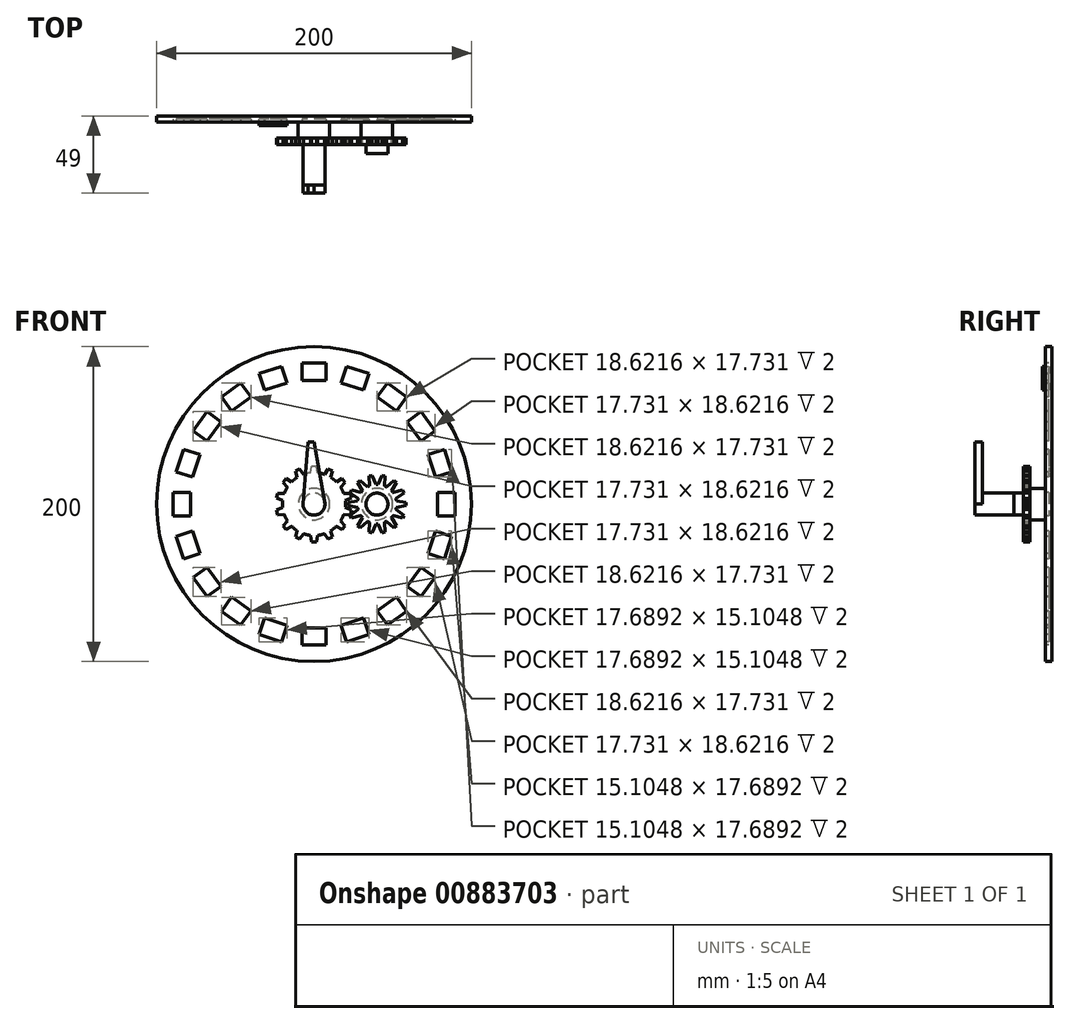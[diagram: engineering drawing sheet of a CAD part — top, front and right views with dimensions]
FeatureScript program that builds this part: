
annotation { "Feature Type Name" : "Feature", "Feature Type Description" : "" }
export const myFeature = defineFeature(function(context is Context, id is Id, definition is map)
    precondition{}
    {
        {
            var Q0;
            Q0=qCreatedBy(makeId("Front.planeOp"),FACE);
            var sketch = newSketch(context, id + "F0", { "sketchPlane" : qUnion([Q0])});
            skCircle(sketch, "E0", {"center": v(0, 0) * mm, "radius": 100 * mm});
            skSolve(sketch);
        }
        {
            var Q0;
            Q0 = qSketchRegion(id + "F0", true);
            extrude(context, id + "F1", {"entities" : qUnion([Q0]), "depth" : 4 * mm, "offsetDistance" : 25 * mm});
        }
        {
            var Q0;
            Q0=makeQuery(id+"F1.opExtrude","CAP_FACE",FACE,{"disambiguationData":[OSD([sQuery(id+"F0.wireOp",EDGE,"E0")])],"isStart":false});
            var sketch = newSketch(context, id + "F2", { "sketchPlane" : qUnion([Q0])});
            skCircle(sketch, "E1", {"center": v(0, 0) * mm, "radius": 10 * mm});
            skCircle(sketch, "E2", {"center": v(0, 0) * mm, "radius": 7 * mm});
            skCircle(sketch, "E3", {"center": v(40, 0) * mm, "radius": 10 * mm});
            skCircle(sketch, "E4", {"center": v(40, 0) * mm, "radius": 7 * mm});
            skSolve(sketch);
        }
        {
            var Q0;
            Q0 = qSketchRegion(id + "F2", true);
            extrude(context, id + "F3", {"entities" : qUnion([Q0]), "operationType" : NewBodyOperationType.ADD, "depth" : 10 * mm, "offsetDistance" : 25 * mm});
        }
        {
            var Q0;
            Q0=makeQuery(id+"F3.boolean.opBoolean","SPLIT",FACE,{"disambiguationData":[TD([makeQuery(id+"F3.opExtrude","SWEPT_FACE",FACE,{"disambiguationData":[OSD([sQuery(id+"F2.wireOp",EDGE,"E2")])]})])],"derivedFrom":makeQuery(id+"F1.opExtrude","CAP_FACE",FACE,{"disambiguationData":[OSD([sQuery(id+"F0.wireOp",EDGE,"E0")])],"isStart":false})});
            extrude(context, id + "F4", {"entities" : qUnion([Q0]), "depth" : 40 * mm, "offsetDistance" : 25 * mm});
        }
        {
            var Q0;
            Q0=makeQuery(id+"F3.boolean.opBoolean","SPLIT",FACE,{"disambiguationData":[TD([makeQuery(id+"F3.opExtrude","SWEPT_FACE",FACE,{"disambiguationData":[OSD([sQuery(id+"F2.wireOp",EDGE,"E4")])]})])],"derivedFrom":makeQuery(id+"F1.opExtrude","CAP_FACE",FACE,{"disambiguationData":[OSD([sQuery(id+"F0.wireOp",EDGE,"E0")])],"isStart":false})});
            extrude(context, id + "F5", {"entities" : qUnion([Q0]), "depth" : 20 * mm, "offsetDistance" : 25 * mm});
        }
        {
            var Q0;
            Q0=makeQuery(id+"F3.opExtrude","CAP_FACE",FACE,{"disambiguationData":[OSD([sQuery(id+"F2.wireOp",EDGE,"E1"),sQuery(id+"F2.wireOp",EDGE,"E2")])],"isStart":false});
            var sketch = newSketch(context, id + "F6", { "sketchPlane" : qUnion([Q0])});
            skCircle(sketch, "E5", {"center": v(0, 0) * mm, "radius": 20 * mm});
            skLineSegment(sketch, "E6", {"start": v(2.23, 19.88) * mm, "end": v(1.5, 24) * mm});
            skLineSegment(sketch, "E7", {"start": v(1.5, 24) * mm, "end": v(0, 24) * mm});
            skLineSegment(sketch, "E8.MirrorCS", {"start": v(-1.5, 24) * mm, "end": v(0, 24) * mm});
            skLineSegment(sketch, "E9.MirrorCS", {"start": v(-2.23, 19.88) * mm, "end": v(-1.5, 24) * mm});
            skLineSegment(sketch, "E10.1.0", {"start": v(-10.63, 16.94) * mm, "end": v(-11.76, 20.97) * mm});
            skLineSegment(sketch, "E10.1.1", {"start": v(-11.76, 20.97) * mm, "end": v(-10.41, 21.62) * mm});
            skLineSegment(sketch, "E10.1.2", {"start": v(-9.06, 22.27) * mm, "end": v(-10.41, 21.62) * mm});
            skLineSegment(sketch, "E10.1.3", {"start": v(-6.62, 18.87) * mm, "end": v(-9.06, 22.27) * mm});
            skLineSegment(sketch, "E10.2.0", {"start": v(-16.93, 10.65) * mm, "end": v(-19.7, 13.8) * mm});
            skLineSegment(sketch, "E10.2.1", {"start": v(-19.7, 13.8) * mm, "end": v(-18.76, 14.96) * mm});
            skLineSegment(sketch, "E10.2.2", {"start": v(-17.83, 16.14) * mm, "end": v(-18.76, 14.96) * mm});
            skLineSegment(sketch, "E10.2.3", {"start": v(-14.15, 14.13) * mm, "end": v(-17.83, 16.14) * mm});
            skLineSegment(sketch, "E11.1.3.0", {"start": v(-19.87, 2.25) * mm, "end": v(-23.73, 3.88) * mm});
            skLineSegment(sketch, "E11.3.3.0", {"start": v(-23.73, 3.88) * mm, "end": v(-23.4, 5.34) * mm});
            skLineSegment(sketch, "E11.6.3.0", {"start": v(-23.06, 6.8) * mm, "end": v(-23.4, 5.34) * mm});
            skLineSegment(sketch, "E11.9.3.0", {"start": v(-18.88, 6.6) * mm, "end": v(-23.06, 6.8) * mm});
            skLineSegment(sketch, "E11.1.4.0", {"start": v(-18.88, -6.6) * mm, "end": v(-23.06, -6.8) * mm});
            skLineSegment(sketch, "E11.3.4.0", {"start": v(-23.06, -6.8) * mm, "end": v(-23.4, -5.34) * mm});
            skLineSegment(sketch, "E11.6.4.0", {"start": v(-23.73, -3.88) * mm, "end": v(-23.4, -5.34) * mm});
            skLineSegment(sketch, "E11.9.4.0", {"start": v(-19.87, -2.25) * mm, "end": v(-23.73, -3.88) * mm});
            skLineSegment(sketch, "E11.1.5.0", {"start": v(-14.15, -14.13) * mm, "end": v(-17.83, -16.14) * mm});
            skLineSegment(sketch, "E11.3.5.0", {"start": v(-17.83, -16.14) * mm, "end": v(-18.76, -14.96) * mm});
            skLineSegment(sketch, "E11.6.5.0", {"start": v(-19.7, -13.8) * mm, "end": v(-18.76, -14.96) * mm});
            skLineSegment(sketch, "E11.9.5.0", {"start": v(-16.93, -10.65) * mm, "end": v(-19.7, -13.8) * mm});
            skLineSegment(sketch, "E11.1.6.0", {"start": v(-6.62, -18.87) * mm, "end": v(-9.06, -22.27) * mm});
            skLineSegment(sketch, "E11.3.6.0", {"start": v(-9.06, -22.27) * mm, "end": v(-10.41, -21.62) * mm});
            skLineSegment(sketch, "E11.6.6.0", {"start": v(-11.76, -20.97) * mm, "end": v(-10.41, -21.62) * mm});
            skLineSegment(sketch, "E11.9.6.0", {"start": v(-10.63, -16.94) * mm, "end": v(-11.76, -20.97) * mm});
            skLineSegment(sketch, "E11.1.7.0", {"start": v(2.23, -19.88) * mm, "end": v(1.5, -24) * mm});
            skLineSegment(sketch, "E11.3.7.0", {"start": v(1.5, -24) * mm, "end": v(0, -24) * mm});
            skLineSegment(sketch, "E11.6.7.0", {"start": v(-1.5, -24) * mm, "end": v(0, -24) * mm});
            skLineSegment(sketch, "E11.9.7.0", {"start": v(-2.23, -19.88) * mm, "end": v(-1.5, -24) * mm});
            skLineSegment(sketch, "E11.1.8.0", {"start": v(10.63, -16.94) * mm, "end": v(11.76, -20.97) * mm});
            skLineSegment(sketch, "E11.3.8.0", {"start": v(11.76, -20.97) * mm, "end": v(10.41, -21.62) * mm});
            skLineSegment(sketch, "E11.6.8.0", {"start": v(9.06, -22.27) * mm, "end": v(10.41, -21.62) * mm});
            skLineSegment(sketch, "E11.9.8.0", {"start": v(6.62, -18.87) * mm, "end": v(9.06, -22.27) * mm});
            skLineSegment(sketch, "E11.1.9.0", {"start": v(16.93, -10.65) * mm, "end": v(19.7, -13.8) * mm});
            skLineSegment(sketch, "E11.3.9.0", {"start": v(19.7, -13.8) * mm, "end": v(18.76, -14.96) * mm});
            skLineSegment(sketch, "E11.6.9.0", {"start": v(17.83, -16.14) * mm, "end": v(18.76, -14.96) * mm});
            skLineSegment(sketch, "E11.9.9.0", {"start": v(14.15, -14.13) * mm, "end": v(17.83, -16.14) * mm});
            skLineSegment(sketch, "E12.1.10.0", {"start": v(19.87, -2.25) * mm, "end": v(23.73, -3.88) * mm});
            skLineSegment(sketch, "E12.3.10.0", {"start": v(23.73, -3.88) * mm, "end": v(23.4, -5.34) * mm});
            skLineSegment(sketch, "E12.6.10.0", {"start": v(23.06, -6.8) * mm, "end": v(23.4, -5.34) * mm});
            skLineSegment(sketch, "E12.9.10.0", {"start": v(18.88, -6.6) * mm, "end": v(23.06, -6.8) * mm});
            skLineSegment(sketch, "E12.1.11.0", {"start": v(18.88, 6.6) * mm, "end": v(23.06, 6.8) * mm});
            skLineSegment(sketch, "E12.3.11.0", {"start": v(23.06, 6.8) * mm, "end": v(23.4, 5.34) * mm});
            skLineSegment(sketch, "E12.6.11.0", {"start": v(23.73, 3.88) * mm, "end": v(23.4, 5.34) * mm});
            skLineSegment(sketch, "E12.9.11.0", {"start": v(19.87, 2.25) * mm, "end": v(23.73, 3.88) * mm});
            skLineSegment(sketch, "E12.1.12.0", {"start": v(14.15, 14.13) * mm, "end": v(17.83, 16.14) * mm});
            skLineSegment(sketch, "E12.3.12.0", {"start": v(17.83, 16.14) * mm, "end": v(18.76, 14.96) * mm});
            skLineSegment(sketch, "E12.6.12.0", {"start": v(19.7, 13.8) * mm, "end": v(18.76, 14.96) * mm});
            skLineSegment(sketch, "E12.9.12.0", {"start": v(16.93, 10.65) * mm, "end": v(19.7, 13.8) * mm});
            skLineSegment(sketch, "E12.1.13.0", {"start": v(6.62, 18.87) * mm, "end": v(9.06, 22.27) * mm});
            skLineSegment(sketch, "E12.3.13.0", {"start": v(9.06, 22.27) * mm, "end": v(10.41, 21.62) * mm});
            skLineSegment(sketch, "E12.6.13.0", {"start": v(11.76, 20.97) * mm, "end": v(10.41, 21.62) * mm});
            skLineSegment(sketch, "E12.9.13.0", {"start": v(10.63, 16.94) * mm, "end": v(11.76, 20.97) * mm});
            skSolve(sketch);
        }
        {
            var Q0;
            Q0 = qSketchRegion(id + "F6", true);
            extrude(context, id + "F7", {"entities" : qUnion([Q0]), "operationType" : NewBodyOperationType.ADD, "depth" : 4 * mm, "offsetDistance" : 25 * mm});
        }
        {
            var Q0;
            Q0=makeQuery(id+"F3.opExtrude","CAP_FACE",FACE,{"disambiguationData":[OSD([sQuery(id+"F2.wireOp",EDGE,"E3"),sQuery(id+"F2.wireOp",EDGE,"E4")])],"isStart":false});
            var sketch = newSketch(context, id + "F8", { "sketchPlane" : qUnion([Q0])});
            skCircle(sketch, "E13", {"center": v(40, 0) * mm, "radius": 12.5 * mm});
            skLineSegment(sketch, "E14", {"start": v(27.67, 2.08) * mm, "end": v(21.53, 1) * mm});
            skLineSegment(sketch, "E15", {"start": v(21.53, 1) * mm, "end": v(21.53, 0) * mm});
            skLineSegment(sketch, "E16.MirrorCS", {"start": v(21.53, -1) * mm, "end": v(21.53, 0) * mm});
            skLineSegment(sketch, "E17.MirrorCS", {"start": v(27.67, -2.08) * mm, "end": v(21.53, -1) * mm});
            skLineSegment(sketch, "E18.1.0", {"start": v(29.8, -7.23) * mm, "end": v(23.8, -8.92) * mm});
            skLineSegment(sketch, "E18.1.1", {"start": v(23.8, -8.92) * mm, "end": v(23.36, -8.02) * mm});
            skLineSegment(sketch, "E18.1.2", {"start": v(22.92, -7.11) * mm, "end": v(23.36, -8.02) * mm});
            skLineSegment(sketch, "E18.1.3", {"start": v(28, -3.47) * mm, "end": v(22.92, -7.11) * mm});
            skLineSegment(sketch, "E18.2.0", {"start": v(33.94, -10.94) * mm, "end": v(29.26, -15.07) * mm});
            skLineSegment(sketch, "E18.2.1", {"start": v(29.26, -15.07) * mm, "end": v(28.48, -14.44) * mm});
            skLineSegment(sketch, "E18.2.2", {"start": v(27.7, -13.82) * mm, "end": v(28.48, -14.44) * mm});
            skLineSegment(sketch, "E18.2.3", {"start": v(30.69, -8.34) * mm, "end": v(27.7, -13.82) * mm});
            skLineSegment(sketch, "E19.2.3.0", {"start": v(39.29, -12.48) * mm, "end": v(36.86, -18.23) * mm});
            skLineSegment(sketch, "E19.3.3.0", {"start": v(36.86, -18.23) * mm, "end": v(35.89, -18) * mm});
            skLineSegment(sketch, "E19.6.3.0", {"start": v(34.91, -17.79) * mm, "end": v(35.89, -18) * mm});
            skLineSegment(sketch, "E19.9.3.0", {"start": v(35.23, -11.55) * mm, "end": v(34.91, -17.79) * mm});
            skLineSegment(sketch, "E19.2.4.0", {"start": v(44.77, -11.55) * mm, "end": v(45.09, -17.79) * mm});
            skLineSegment(sketch, "E19.3.4.0", {"start": v(45.09, -17.79) * mm, "end": v(44.11, -18) * mm});
            skLineSegment(sketch, "E19.6.4.0", {"start": v(43.14, -18.23) * mm, "end": v(44.11, -18) * mm});
            skLineSegment(sketch, "E19.9.4.0", {"start": v(40.71, -12.48) * mm, "end": v(43.14, -18.23) * mm});
            skLineSegment(sketch, "E20.2.5.0", {"start": v(49.31, -8.34) * mm, "end": v(52.3, -13.82) * mm});
            skLineSegment(sketch, "E20.3.5.0", {"start": v(52.3, -13.82) * mm, "end": v(51.52, -14.44) * mm});
            skLineSegment(sketch, "E20.6.5.0", {"start": v(50.74, -15.07) * mm, "end": v(51.52, -14.44) * mm});
            skLineSegment(sketch, "E20.9.5.0", {"start": v(46.06, -10.94) * mm, "end": v(50.74, -15.07) * mm});
            skLineSegment(sketch, "E20.2.6.0", {"start": v(52, -3.47) * mm, "end": v(57.08, -7.11) * mm});
            skLineSegment(sketch, "E20.3.6.0", {"start": v(57.08, -7.11) * mm, "end": v(56.64, -8.02) * mm});
            skLineSegment(sketch, "E20.6.6.0", {"start": v(56.2, -8.92) * mm, "end": v(56.64, -8.02) * mm});
            skLineSegment(sketch, "E20.9.6.0", {"start": v(50.2, -7.23) * mm, "end": v(56.2, -8.92) * mm});
            skLineSegment(sketch, "E20.2.7.0", {"start": v(52.33, 2.08) * mm, "end": v(58.47, 1) * mm});
            skLineSegment(sketch, "E20.3.7.0", {"start": v(58.47, 1) * mm, "end": v(58.47, 0) * mm});
            skLineSegment(sketch, "E20.6.7.0", {"start": v(58.47, -1) * mm, "end": v(58.47, 0) * mm});
            skLineSegment(sketch, "E20.9.7.0", {"start": v(52.33, -2.08) * mm, "end": v(58.47, -1) * mm});
            skLineSegment(sketch, "E20.2.8.0", {"start": v(50.2, 7.23) * mm, "end": v(56.2, 8.92) * mm});
            skLineSegment(sketch, "E20.3.8.0", {"start": v(56.2, 8.92) * mm, "end": v(56.64, 8.02) * mm});
            skLineSegment(sketch, "E20.6.8.0", {"start": v(57.08, 7.11) * mm, "end": v(56.64, 8.02) * mm});
            skLineSegment(sketch, "E20.9.8.0", {"start": v(52, 3.47) * mm, "end": v(57.08, 7.11) * mm});
            skLineSegment(sketch, "E20.2.9.0", {"start": v(46.06, 10.94) * mm, "end": v(50.74, 15.07) * mm});
            skLineSegment(sketch, "E20.3.9.0", {"start": v(50.74, 15.07) * mm, "end": v(51.52, 14.44) * mm});
            skLineSegment(sketch, "E20.6.9.0", {"start": v(52.3, 13.82) * mm, "end": v(51.52, 14.44) * mm});
            skLineSegment(sketch, "E20.9.9.0", {"start": v(49.31, 8.34) * mm, "end": v(52.3, 13.82) * mm});
            skLineSegment(sketch, "E21.2.10.0", {"start": v(40.71, 12.48) * mm, "end": v(43.14, 18.23) * mm});
            skLineSegment(sketch, "E21.3.10.0", {"start": v(43.14, 18.23) * mm, "end": v(44.11, 18) * mm});
            skLineSegment(sketch, "E21.6.10.0", {"start": v(45.09, 17.79) * mm, "end": v(44.11, 18) * mm});
            skLineSegment(sketch, "E21.9.10.0", {"start": v(44.77, 11.55) * mm, "end": v(45.09, 17.79) * mm});
            skLineSegment(sketch, "E21.2.11.0", {"start": v(35.23, 11.55) * mm, "end": v(34.91, 17.79) * mm});
            skLineSegment(sketch, "E21.3.11.0", {"start": v(34.91, 17.79) * mm, "end": v(35.89, 18) * mm});
            skLineSegment(sketch, "E21.6.11.0", {"start": v(36.86, 18.23) * mm, "end": v(35.89, 18) * mm});
            skLineSegment(sketch, "E21.9.11.0", {"start": v(39.29, 12.48) * mm, "end": v(36.86, 18.23) * mm});
            skLineSegment(sketch, "E21.2.12.0", {"start": v(30.69, 8.34) * mm, "end": v(27.7, 13.82) * mm});
            skLineSegment(sketch, "E21.3.12.0", {"start": v(27.7, 13.82) * mm, "end": v(28.48, 14.44) * mm});
            skLineSegment(sketch, "E21.6.12.0", {"start": v(29.26, 15.07) * mm, "end": v(28.48, 14.44) * mm});
            skLineSegment(sketch, "E21.9.12.0", {"start": v(33.94, 10.94) * mm, "end": v(29.26, 15.07) * mm});
            skLineSegment(sketch, "E21.2.13.0", {"start": v(28, 3.47) * mm, "end": v(22.92, 7.11) * mm});
            skLineSegment(sketch, "E21.3.13.0", {"start": v(22.92, 7.11) * mm, "end": v(23.36, 8.02) * mm});
            skLineSegment(sketch, "E21.6.13.0", {"start": v(23.8, 8.92) * mm, "end": v(23.36, 8.02) * mm});
            skLineSegment(sketch, "E21.9.13.0", {"start": v(29.8, 7.23) * mm, "end": v(23.8, 8.92) * mm});
            skSolve(sketch);
        }
        {
            var Q0;
            Q0 = qSketchRegion(id + "F8", true);
            extrude(context, id + "F9", {"entities" : qUnion([Q0]), "operationType" : NewBodyOperationType.ADD, "depth" : 4 * mm, "offsetDistance" : 25 * mm});
        }
        {
            var Q0;
            {var subQ0=sQuery(id+"F0.wireOp",EDGE,"E0");Q0=makeQuery(id+"F3.boolean.opBoolean","SPLIT",FACE,{"disambiguationData":[TD([makeQuery(id+"F1.opExtrude","SWEPT_FACE",FACE,{"disambiguationData":[OSD([subQ0])]})])],"derivedFrom":makeQuery(id+"F1.opExtrude","CAP_FACE",FACE,{"disambiguationData":[OSD([subQ0])],"isStart":false})});}
            var sketch = newSketch(context, id + "F10", { "sketchPlane" : qUnion([Q0])});
            skLineSegment(sketch, "E22.bottom", {"start": v(7.51, 78.55) * mm, "end": v(-7.51, 78.55) * mm});
            skLineSegment(sketch, "E22.top", {"start": v(7.51, 89.55) * mm, "end": v(-7.51, 89.55) * mm});
            skLineSegment(sketch, "E22.left", {"start": v(7.51, 78.55) * mm, "end": v(7.51, 89.55) * mm});
            skLineSegment(sketch, "E22.right", {"start": v(-7.51, 78.55) * mm, "end": v(-7.51, 89.55) * mm});
            skPoint(sketch, "E22.middle", {"position": v(0, 84.05) * mm});
            skLineSegment(sketch, "E23.1.0", {"start": v(-20.53, 87.49) * mm, "end": v(-34.82, 82.85) * mm});
            skLineSegment(sketch, "E23.1.1", {"start": v(-31.42, 72.38) * mm, "end": v(-34.82, 82.85) * mm});
            skLineSegment(sketch, "E23.1.2", {"start": v(-17.13, 77.03) * mm, "end": v(-20.53, 87.49) * mm});
            skLineSegment(sketch, "E23.1.3", {"start": v(-17.13, 77.03) * mm, "end": v(-31.42, 72.38) * mm});
            skLineSegment(sketch, "E23.2.0", {"start": v(-46.56, 76.86) * mm, "end": v(-58.71, 68.03) * mm});
            skLineSegment(sketch, "E23.2.1", {"start": v(-52.25, 59.13) * mm, "end": v(-58.71, 68.03) * mm});
            skLineSegment(sketch, "E23.2.2", {"start": v(-40.1, 67.96) * mm, "end": v(-46.56, 76.86) * mm});
            skLineSegment(sketch, "E23.2.3", {"start": v(-40.1, 67.96) * mm, "end": v(-52.25, 59.13) * mm});
            skPoint(sketch, "E23.center", {"position": v(0, 0) * mm});
            skLineSegment(sketch, "E24.2.3.0", {"start": v(-68.03, 58.71) * mm, "end": v(-76.86, 46.56) * mm});
            skLineSegment(sketch, "E24.3.3.0", {"start": v(-67.96, 40.1) * mm, "end": v(-76.86, 46.56) * mm});
            skLineSegment(sketch, "E24.6.3.0", {"start": v(-59.13, 52.25) * mm, "end": v(-68.03, 58.71) * mm});
            skLineSegment(sketch, "E24.9.3.0", {"start": v(-59.13, 52.25) * mm, "end": v(-67.96, 40.1) * mm});
            skLineSegment(sketch, "E24.2.4.0", {"start": v(-82.85, 34.82) * mm, "end": v(-87.49, 20.53) * mm});
            skLineSegment(sketch, "E24.3.4.0", {"start": v(-77.03, 17.13) * mm, "end": v(-87.49, 20.53) * mm});
            skLineSegment(sketch, "E24.6.4.0", {"start": v(-72.38, 31.42) * mm, "end": v(-82.85, 34.82) * mm});
            skLineSegment(sketch, "E24.9.4.0", {"start": v(-72.38, 31.42) * mm, "end": v(-77.03, 17.13) * mm});
            skLineSegment(sketch, "E25.2.5.0", {"start": v(-89.55, 7.51) * mm, "end": v(-89.55, -7.51) * mm});
            skLineSegment(sketch, "E25.3.5.0", {"start": v(-78.55, -7.51) * mm, "end": v(-89.55, -7.51) * mm});
            skLineSegment(sketch, "E25.6.5.0", {"start": v(-78.55, 7.51) * mm, "end": v(-89.55, 7.51) * mm});
            skLineSegment(sketch, "E25.9.5.0", {"start": v(-78.55, 7.51) * mm, "end": v(-78.55, -7.51) * mm});
            skLineSegment(sketch, "E25.2.6.0", {"start": v(-87.49, -20.53) * mm, "end": v(-82.85, -34.82) * mm});
            skLineSegment(sketch, "E25.3.6.0", {"start": v(-72.38, -31.42) * mm, "end": v(-82.85, -34.82) * mm});
            skLineSegment(sketch, "E25.6.6.0", {"start": v(-77.03, -17.13) * mm, "end": v(-87.49, -20.53) * mm});
            skLineSegment(sketch, "E25.9.6.0", {"start": v(-77.03, -17.13) * mm, "end": v(-72.38, -31.42) * mm});
            skLineSegment(sketch, "E25.2.7.0", {"start": v(-76.86, -46.56) * mm, "end": v(-68.03, -58.71) * mm});
            skLineSegment(sketch, "E25.3.7.0", {"start": v(-59.13, -52.25) * mm, "end": v(-68.03, -58.71) * mm});
            skLineSegment(sketch, "E25.6.7.0", {"start": v(-67.96, -40.1) * mm, "end": v(-76.86, -46.56) * mm});
            skLineSegment(sketch, "E25.9.7.0", {"start": v(-67.96, -40.1) * mm, "end": v(-59.13, -52.25) * mm});
            skLineSegment(sketch, "E25.2.8.0", {"start": v(-58.71, -68.03) * mm, "end": v(-46.56, -76.86) * mm});
            skLineSegment(sketch, "E25.3.8.0", {"start": v(-40.1, -67.96) * mm, "end": v(-46.56, -76.86) * mm});
            skLineSegment(sketch, "E25.6.8.0", {"start": v(-52.25, -59.13) * mm, "end": v(-58.71, -68.03) * mm});
            skLineSegment(sketch, "E25.9.8.0", {"start": v(-52.25, -59.13) * mm, "end": v(-40.1, -67.96) * mm});
            skLineSegment(sketch, "E25.2.9.0", {"start": v(-34.82, -82.85) * mm, "end": v(-20.53, -87.49) * mm});
            skLineSegment(sketch, "E25.3.9.0", {"start": v(-17.13, -77.03) * mm, "end": v(-20.53, -87.49) * mm});
            skLineSegment(sketch, "E25.6.9.0", {"start": v(-31.42, -72.38) * mm, "end": v(-34.82, -82.85) * mm});
            skLineSegment(sketch, "E25.9.9.0", {"start": v(-31.42, -72.38) * mm, "end": v(-17.13, -77.03) * mm});
            skLineSegment(sketch, "E25.2.10.0", {"start": v(-7.51, -89.55) * mm, "end": v(7.51, -89.55) * mm});
            skLineSegment(sketch, "E25.3.10.0", {"start": v(7.51, -78.55) * mm, "end": v(7.51, -89.55) * mm});
            skLineSegment(sketch, "E25.6.10.0", {"start": v(-7.51, -78.55) * mm, "end": v(-7.51, -89.55) * mm});
            skLineSegment(sketch, "E25.9.10.0", {"start": v(-7.51, -78.55) * mm, "end": v(7.51, -78.55) * mm});
            skLineSegment(sketch, "E25.2.11.0", {"start": v(20.53, -87.49) * mm, "end": v(34.82, -82.85) * mm});
            skLineSegment(sketch, "E25.3.11.0", {"start": v(31.42, -72.38) * mm, "end": v(34.82, -82.85) * mm});
            skLineSegment(sketch, "E25.6.11.0", {"start": v(17.13, -77.03) * mm, "end": v(20.53, -87.49) * mm});
            skLineSegment(sketch, "E25.9.11.0", {"start": v(17.13, -77.03) * mm, "end": v(31.42, -72.38) * mm});
            skLineSegment(sketch, "E25.2.12.0", {"start": v(46.56, -76.86) * mm, "end": v(58.71, -68.03) * mm});
            skLineSegment(sketch, "E25.3.12.0", {"start": v(52.25, -59.13) * mm, "end": v(58.71, -68.03) * mm});
            skLineSegment(sketch, "E25.6.12.0", {"start": v(40.1, -67.96) * mm, "end": v(46.56, -76.86) * mm});
            skLineSegment(sketch, "E25.9.12.0", {"start": v(40.1, -67.96) * mm, "end": v(52.25, -59.13) * mm});
            skLineSegment(sketch, "E25.2.13.0", {"start": v(68.03, -58.71) * mm, "end": v(76.86, -46.56) * mm});
            skLineSegment(sketch, "E25.3.13.0", {"start": v(67.96, -40.1) * mm, "end": v(76.86, -46.56) * mm});
            skLineSegment(sketch, "E25.6.13.0", {"start": v(59.13, -52.25) * mm, "end": v(68.03, -58.71) * mm});
            skLineSegment(sketch, "E25.9.13.0", {"start": v(59.13, -52.25) * mm, "end": v(67.96, -40.1) * mm});
            skLineSegment(sketch, "E25.2.14.0", {"start": v(82.85, -34.82) * mm, "end": v(87.49, -20.53) * mm});
            skLineSegment(sketch, "E25.3.14.0", {"start": v(77.03, -17.13) * mm, "end": v(87.49, -20.53) * mm});
            skLineSegment(sketch, "E25.6.14.0", {"start": v(72.38, -31.42) * mm, "end": v(82.85, -34.82) * mm});
            skLineSegment(sketch, "E25.9.14.0", {"start": v(72.38, -31.42) * mm, "end": v(77.03, -17.13) * mm});
            skLineSegment(sketch, "E25.2.15.0", {"start": v(89.55, -7.51) * mm, "end": v(89.55, 7.51) * mm});
            skLineSegment(sketch, "E25.3.15.0", {"start": v(78.55, 7.51) * mm, "end": v(89.55, 7.51) * mm});
            skLineSegment(sketch, "E25.6.15.0", {"start": v(78.55, -7.51) * mm, "end": v(89.55, -7.51) * mm});
            skLineSegment(sketch, "E25.9.15.0", {"start": v(78.55, -7.51) * mm, "end": v(78.55, 7.51) * mm});
            skLineSegment(sketch, "E25.2.16.0", {"start": v(87.49, 20.53) * mm, "end": v(82.85, 34.82) * mm});
            skLineSegment(sketch, "E25.3.16.0", {"start": v(72.38, 31.42) * mm, "end": v(82.85, 34.82) * mm});
            skLineSegment(sketch, "E25.6.16.0", {"start": v(77.03, 17.13) * mm, "end": v(87.49, 20.53) * mm});
            skLineSegment(sketch, "E25.9.16.0", {"start": v(77.03, 17.13) * mm, "end": v(72.38, 31.42) * mm});
            skLineSegment(sketch, "E25.2.17.0", {"start": v(76.86, 46.56) * mm, "end": v(68.03, 58.71) * mm});
            skLineSegment(sketch, "E25.3.17.0", {"start": v(59.13, 52.25) * mm, "end": v(68.03, 58.71) * mm});
            skLineSegment(sketch, "E25.6.17.0", {"start": v(67.96, 40.1) * mm, "end": v(76.86, 46.56) * mm});
            skLineSegment(sketch, "E25.9.17.0", {"start": v(67.96, 40.1) * mm, "end": v(59.13, 52.25) * mm});
            skLineSegment(sketch, "E25.2.18.0", {"start": v(58.71, 68.03) * mm, "end": v(46.56, 76.86) * mm});
            skLineSegment(sketch, "E25.3.18.0", {"start": v(40.1, 67.96) * mm, "end": v(46.56, 76.86) * mm});
            skLineSegment(sketch, "E25.6.18.0", {"start": v(52.25, 59.13) * mm, "end": v(58.71, 68.03) * mm});
            skLineSegment(sketch, "E25.9.18.0", {"start": v(52.25, 59.13) * mm, "end": v(40.1, 67.96) * mm});
            skLineSegment(sketch, "E25.2.19.0", {"start": v(34.82, 82.85) * mm, "end": v(20.53, 87.49) * mm});
            skLineSegment(sketch, "E25.3.19.0", {"start": v(17.13, 77.03) * mm, "end": v(20.53, 87.49) * mm});
            skLineSegment(sketch, "E25.6.19.0", {"start": v(31.42, 72.38) * mm, "end": v(34.82, 82.85) * mm});
            skLineSegment(sketch, "E25.9.19.0", {"start": v(31.42, 72.38) * mm, "end": v(17.13, 77.03) * mm});
            skSolve(sketch);
        }
        {
            var Q0;
            Q0 = qSketchRegion(id + "F10", true);
            extrude(context, id + "F11", {"entities" : qUnion([Q0]), "operationType" : NewBodyOperationType.REMOVE, "oppositeDirection" : true, "depth" : 2 * mm, "offsetDistance" : 25 * mm});
        }
        {
            var Q0;
            Q0=makeQuery(id+"F11.boolean.opBoolean","COPY",FACE,{"derivedFrom":makeQuery(id+"F11.opExtrude","CAP_FACE",FACE,{"disambiguationData":[OSD([sQuery(id+"F10.wireOp",EDGE,"E23.1.0"),sQuery(id+"F10.wireOp",EDGE,"E23.1.1"),sQuery(id+"F10.wireOp",EDGE,"E23.1.2"),sQuery(id+"F10.wireOp",EDGE,"E23.1.3")])],"isStart":false})});
            extrude(context, id + "F12", {"entities" : qUnion([Q0]), "depth" : 4 * mm, "offsetDistance" : 25 * mm});
        }
        {
            var Q0;
            Q0=makeQuery(id+"F4.opExtrude","CAP_FACE",FACE,{"disambiguationData":[OSD([sQuery(id+"F0.wireOp",EDGE,"E0")])],"isStart":false});
            var sketch = newSketch(context, id + "F13", { "sketchPlane" : qUnion([Q0])});
            skLineSegment(sketch, "E26", {"start": v(-7, 0) * mm, "end": v(-3.75, 39.38) * mm});
            skLineSegment(sketch, "E27", {"start": v(7, 0) * mm, "end": v(0, 39.38) * mm});
            skLineSegment(sketch, "E28", {"start": v(-3.75, 39.38) * mm, "end": v(0, 39.38) * mm});
            skSolve(sketch);
        }
        {
            var Q0;
            {var subQ0=sQuery(id+"F13.wireOp",EDGE,"E26");Q0=makeQuery(id+"F13.imprint","IMPRINT",FACE,{"disambiguationData":[TD([[makeQuery(id+"F13.imprint","IMPRINT",EDGE,{"derivedFrom":subQ0}),-1.0]])]});}
            var Q1;
            {var subQ0=sQuery(id+"F13.wireOp",EDGE,"E27");var subQ1=makeQuery(id+"F4.opExtrude","CAP_EDGE",EDGE,{"disambiguationData":[OSD([sQuery(id+"F2.wireOp",EDGE,"E2")])],"isStart":false});var subQ2=makeQuery(id+"F13.imprint","INTERSECT",VERTEX,{"disambiguationData":[OD(0.0)],"derivedFrom":[subQ1,subQ0]});Q1=makeQuery(id+"F13.imprint","IMPRINT",FACE,{"disambiguationData":[TD([[makeQuery(id+"F13.imprint","IMPRINT",EDGE,{"disambiguationData":[TD([[subQ2,-1.0]])],"derivedFrom":subQ0}),1.0]])]});}
            extrude(context, id + "F14", {"entities" : qUnion([Q0, Q1]), "operationType" : NewBodyOperationType.ADD, "depth" : 5 * mm, "offsetDistance" : 25 * mm});
        }
    });
